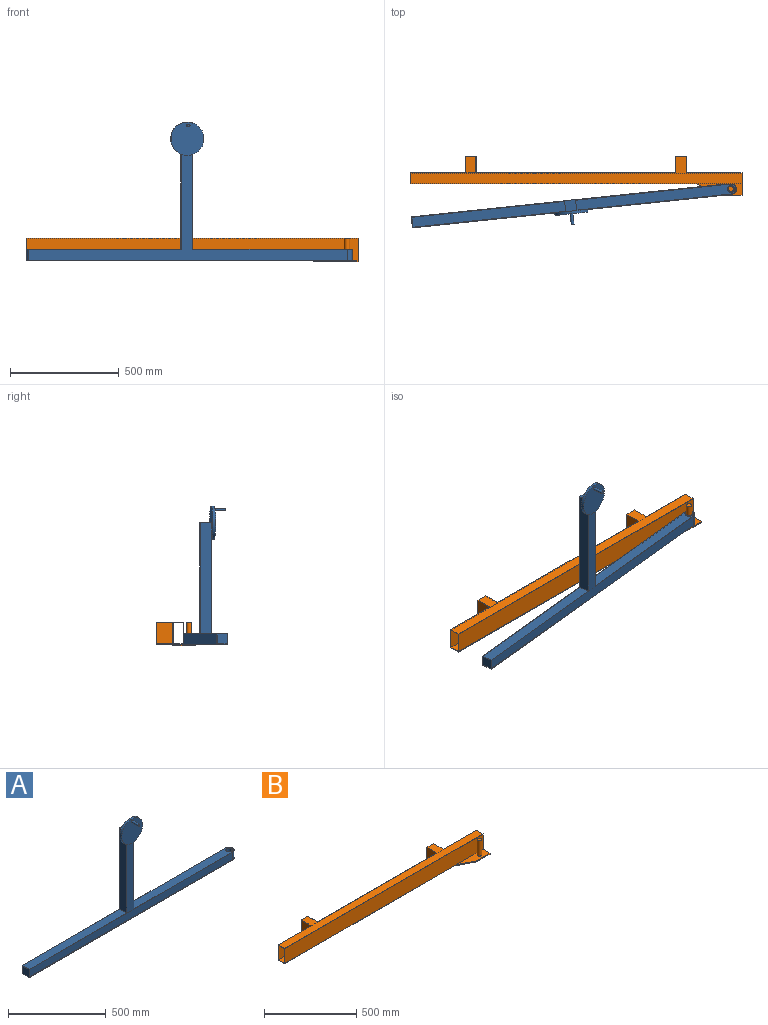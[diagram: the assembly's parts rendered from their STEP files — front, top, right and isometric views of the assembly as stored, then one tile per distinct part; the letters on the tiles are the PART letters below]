
ASSEMBLY  parts=2 mates=1
PART A: 23 faces, bbox 1498.6x114.3x635 mm
  f0: plane 1473.2x486.96mm, normal (0,-1,0), area 96846.9mm2, adj f1,f2,f5,f6,f7,f8,f9,f11
  f1: plane 739.89x50.8mm, normal (0,0,1), area 36696.5mm2, adj f0,f2,f3,f4,f9
  f2: cylinder r=25.4mm len=50.8mm, axis (0,0,-1), area 4053.7mm2, adj f0,f1,f3,f7
  f3: plane 1473.2x558.8mm, normal (0,1,0), area 100645mm2, adj f1,f2,f5,f6,f7,f8,f9,f10
  f4: cylinder r=13.97mm len=50.8mm, axis (0,0,-1), area 4459mm2, adj f1,f7
  f5: plane 50.8x50.8mm, normal (-1,0,0), area 2580.6mm2, adj f0,f3,f6,f7
  f6: plane 707.91x50.8mm, normal (0,0,1), area 35961.7mm2, adj f0,f3,f5,f8
  f7: plane 1498.6x50.8mm, normal (0,0,-1), area 75238.9mm2, adj f0,f2,f3,f4,f5
  f8: plane 508x50.8mm, normal (-1,0,0), area 25806.4mm2, adj f0,f3,f6,f10,f13
  f9: plane 508x50.8mm, normal (1,0,0), area 25806.4mm2, adj f0,f1,f3,f10,f13
  f10: plane 50.8x50.8mm, normal (0,0,1), area 2580.6mm2, adj f3,f8,f9,f13
  f11: cylinder r=76.2mm len=152.4mm, axis (0,1,0), area 6080.5mm2, adj f0,f12,f13
  f12: plane 152.4x152.4mm, normal (0,-1,0), area 18114.8mm2, adj f11,f14
  f13: plane 152.4x148.04mm, normal (0,1,0), area 14443.4mm2, adj f8,f9,f10,f11
  f14: cylinder r=6.35mm len=50.8mm, axis (0,1,0), area 2026.8mm2, adj f12,f15
  f15: plane 12.7x12.7mm, normal (0,-1,0), area 126.7mm2, adj f14
  f16: plane 1470.66x45.72mm, normal (0,1,0), area 67238.6mm2, adj f17,f20,f21,f22
  f17: cylinder r=22.86mm len=45.72mm, axis (0,0,-1), area 3283.5mm2, adj f16,f18,f21,f22
  f18: plane 1470.66x45.72mm, normal (0,-1,0), area 67238.6mm2, adj f17,f20,f21,f22
  f19: cylinder r=16.51mm len=45.72mm, axis (0,0,-1), area 4742.8mm2, adj f21,f22
  f20: plane 45.72x45.72mm, normal (1,0,0), area 2090.3mm2, adj f16,f18,f21,f22
  f21: plane 1493.52x45.72mm, normal (0,0,-1), area 67203.1mm2, adj f16,f17,f18,f19,f20
  f22: plane 1493.52x45.72mm, normal (0,0,1), area 67203.1mm2, adj f16,f17,f18,f19,f20
PART B: 30 faces, bbox 1524x180.3x108 mm
  f0: plane 914.4x101.6mm, normal (0,1,0), area 92903mm2, adj f4,f6,f12,f21
  f1: plane 254x107.95mm, normal (0,1,0), area 27096.7mm2, adj f3,f4,f6,f20,f23,f26
  f2: plane 101.6x50.8mm, normal (-1,0,0), area 748.4mm2, adj f4,f5,f6,f7,f8,f9,f10,f11
  f3: plane 107.95x104.12mm, normal (1,0,0), area 1409.5mm2, adj f1,f6,f7,f8,f9,f10,f11,f24
  f4: plane 1320.8x127mm, normal (0,0,-1), area 74838.6mm2, adj f0,f1,f2,f5,f7,f12,f13,f14
  f5: plane 254x101.6mm, normal (0,1,0), area 25806.4mm2, adj f2,f4,f6,f13
  f6: plane 1524x127mm, normal (0,0,1), area 85161.1mm2, adj f0,f1,f2,f3,f5,f7,f12,f13
  f7: plane 1524x101.6mm, normal (0,-1,0), area 154838.4mm2, adj f2,f3,f4,f6,f27
  f8: plane 1524x45.72mm, normal (0,0,1), area 69677.3mm2, adj f2,f3,f9,f11
  f9: plane 1524x96.52mm, normal (0,-1,0), area 147096.5mm2, adj f2,f3,f8,f10
  f10: plane 1524x45.72mm, normal (0,0,-1), area 69677.3mm2, adj f2,f3,f9,f11
  f11: plane 1524x96.52mm, normal (0,1,0), area 147096.5mm2, adj f2,f3,f8,f10
  f12: plane 101.6x76.2mm, normal (1,0,0), area 7741.9mm2, adj f0,f4,f6,f14
  f13: plane 101.6x76.2mm, normal (-1,0,0), area 7741.9mm2, adj f4,f5,f6,f14
  f14: plane 101.6x50.8mm, normal (0,1,0), area 748.4mm2, adj f4,f6,f12,f13,f16,f17,f18,f19
  f15: plane 96.52x45.72mm, normal (0,1,0), area 4412.9mm2, adj f16,f17,f18,f19
  f16: plane 76.2x45.72mm, normal (0,0,1), area 3483.9mm2, adj f14,f15,f18,f19
  f17: plane 76.2x45.72mm, normal (0,0,-1), area 3483.9mm2, adj f14,f15,f18,f19
  f18: plane 96.52x76.2mm, normal (-1,0,0), area 7354.8mm2, adj f14,f15,f16,f17
  f19: plane 96.52x76.2mm, normal (1,0,0), area 7354.8mm2, adj f14,f15,f16,f17
  f20: plane 101.6x76.2mm, normal (1,0,0), area 7741.9mm2, adj f1,f4,f6,f22
  f21: plane 101.6x76.2mm, normal (-1,0,0), area 7741.9mm2, adj f0,f4,f6,f22
  f22: plane 101.6x50.8mm, normal (0,1,0), area 5161.3mm2, adj f4,f6,f20,f21
  f23: plane 52.06x6.35mm, normal (-1,0,0), area 330.6mm2, adj f1,f4,f25,f26,f27
  f24: plane 101.6x6.35mm, normal (0,-1,0), area 645.2mm2, adj f3,f25,f26,f27
  f25: plane 101.6x52.06mm, normal (-0.46,-0.89,0), area 724.9mm2, adj f23,f24,f26,f27
  f26: plane 203.2x104.12mm, normal (0,0,-1), area 18512.2mm2, adj f1,f3,f23,f24,f25
  f27: plane 203.2x53.32mm, normal (0,0,1), area 7682.9mm2, adj f3,f7,f23,f24,f25,f28
  f28: cylinder r=12.7mm len=101.6mm, axis (0,0,-1), area 8107.3mm2, adj f27,f29
  f29: plane 25.4x25.4mm, normal (0,0,1), area 506.7mm2, adj f28
PLACE A rot(axis=(0,0,1),6deg) t=(-24.68,-151.58,25.4)mm
PLACE B t=(0,-25.4,50.8)mm
MATE cylindrical A.f2 <-> B.f28  axis (0,0,1) through (711.2,-74.61,50.8)mm
